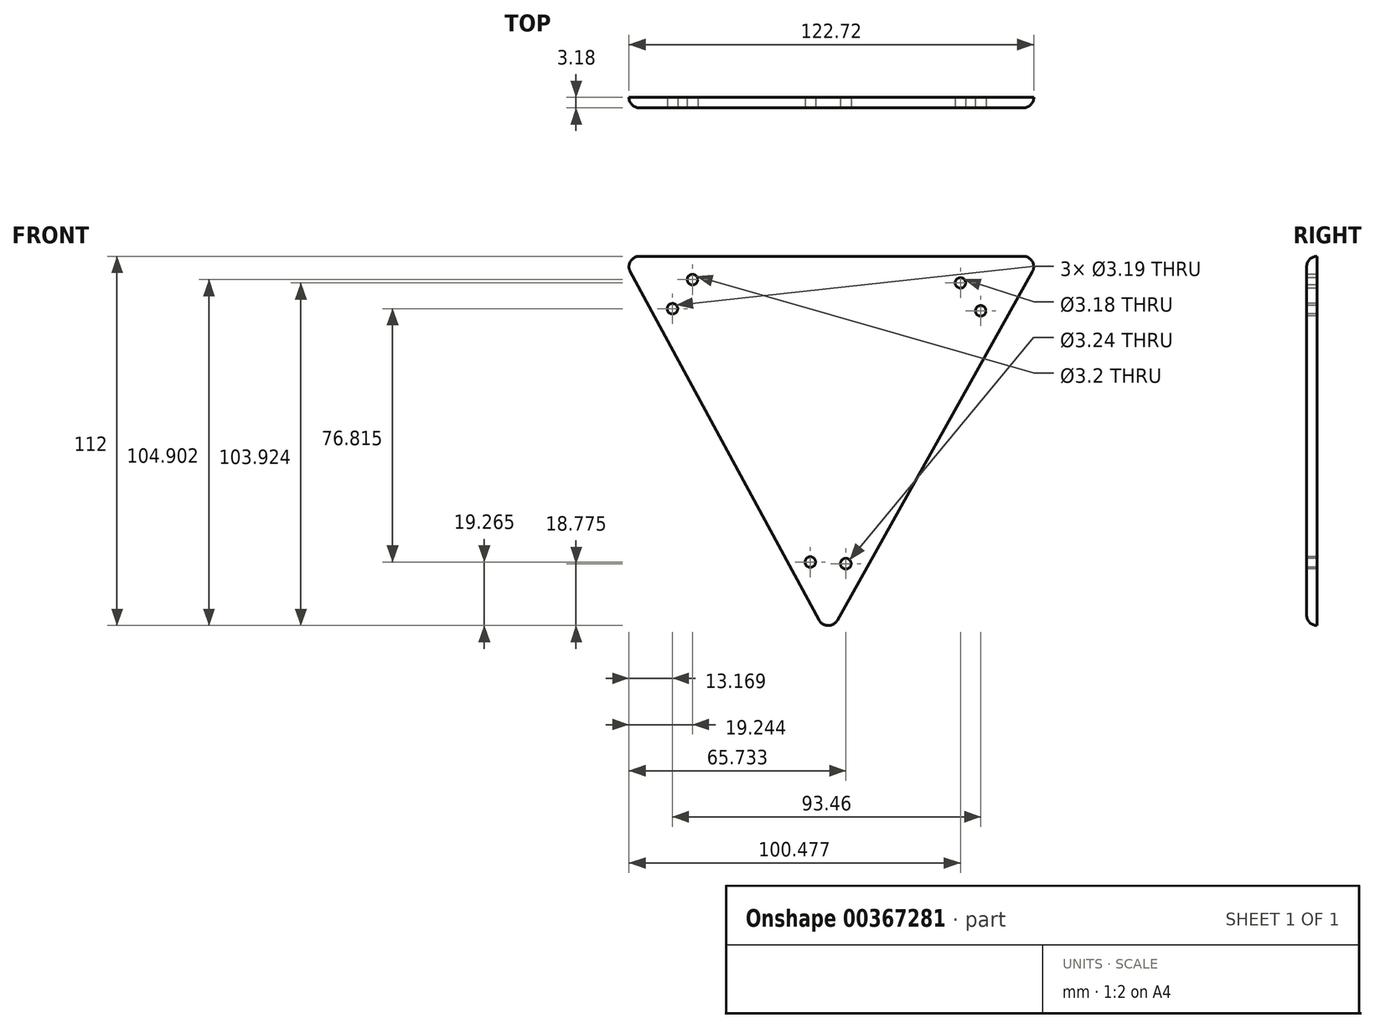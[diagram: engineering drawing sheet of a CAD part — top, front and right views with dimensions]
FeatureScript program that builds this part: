
annotation { "Feature Type Name" : "Feature", "Feature Type Description" : "" }
export const myFeature = defineFeature(function(context is Context, id is Id, definition is map)
    precondition{}
    {
        {
            var Q0;
            Q0=qCreatedBy(makeId("Front.planeOp"),FACE);
            var sketch = newSketch(context, id + "F0", { "sketchPlane" : qUnion([Q0])});
            skLineSegment(sketch, "E0", {"start": v(-62.51, 39.64) * mm, "end": v(64.6, 39.64) * mm});
            skLineSegment(sketch, "E1", {"start": v(64.6, 39.64) * mm, "end": v(0, -75.77) * mm});
            skLineSegment(sketch, "E2", {"start": v(-62.51, 39.64) * mm, "end": v(0, -75.77) * mm});
            skCircle(sketch, "E3", {"center": v(-41.1, 32.54) * mm, "radius": 1.6 * mm});
            skCircle(sketch, "E4", {"center": v(-47.18, 23.72) * mm, "radius": 1.6 * mm});
            skCircle(sketch, "E5", {"center": v(46.28, 23.1) * mm, "radius": 1.6 * mm});
            skCircle(sketch, "E6", {"center": v(5.38, -53.58) * mm, "radius": 1.62 * mm});
            skCircle(sketch, "E7", {"center": v(40.13, 31.56) * mm, "radius": 1.59 * mm});
            skCircle(sketch, "E8", {"center": v(7.83, 33.52) * mm, "radius": 1.58 * mm});
            skCircle(sketch, "E9", {"center": v(-5.38, -53.1) * mm, "radius": 1.6 * mm});
            skCircle(sketch, "E10", {"center": v(-6.85, 33.52) * mm, "radius": 1.57 * mm});
            skSolve(sketch);
        }
        {
            var Q0;
            Q0=qSketchRegion(id+"F0",true);
            var Q1;
            Q1=makeQuery(id+"F0.imprint","IMPRINT",FACE,{"disambiguationData":[TD([[makeQuery(id+"F0.imprint","IMPRINT",EDGE,{"derivedFrom":sQuery(id+"F0.wireOp",EDGE,"E8")}),1.0]])]});
            var Q2;
            Q2=makeQuery(id+"F0.imprint","IMPRINT",FACE,{"disambiguationData":[TD([[makeQuery(id+"F0.imprint","IMPRINT",EDGE,{"derivedFrom":sQuery(id+"F0.wireOp",EDGE,"E10")}),1.0]])]});
            extrude(context, id + "F1", {"entities" : qUnion([Q0, Q1, Q2]), "oppositeDirection" : true, "depth" : 3.17 * mm});
        }
        {
            var Q0;
            Q0=makeQuery(id+"F1.opExtrude","SWEPT_EDGE",EDGE,{"disambiguationData":[OSD([sQuery(id+"F0.wireOp",EDGE,"E0"),sQuery(id+"F0.wireOp",EDGE,"E1")])]});
            var Q1;
            Q1=makeQuery(id+"F1.opExtrude","SWEPT_EDGE",EDGE,{"disambiguationData":[OSD([sQuery(id+"F0.wireOp",EDGE,"E0"),sQuery(id+"F0.wireOp",EDGE,"E2")])]});
            var Q2;
            Q2=makeQuery(id+"F1.opExtrude","SWEPT_EDGE",EDGE,{"disambiguationData":[OSD([sQuery(id+"F0.wireOp",EDGE,"E1"),sQuery(id+"F0.wireOp",EDGE,"E2")])]});
            var Q3;
            Q3=makeQuery(id+"F1.opExtrude","CAP_EDGE",EDGE,{"disambiguationData":[OSD([sQuery(id+"F0.wireOp",EDGE,"E2")])],"isStart":true});
            var Q4;
            Q4=makeQuery(id+"F1.opExtrude","CAP_EDGE",EDGE,{"disambiguationData":[OSD([sQuery(id+"F0.wireOp",EDGE,"E1")])],"isStart":true});
            var Q5;
            Q5=makeQuery(id+"F1.opExtrude","CAP_EDGE",EDGE,{"disambiguationData":[OSD([sQuery(id+"F0.wireOp",EDGE,"E0")])],"isStart":true});
            fillet(context, id + "F2", {"entities" : qUnion([Q0, Q1, Q2, Q3, Q4, Q5]), "radius" : 3.17 * mm, "tangentPropagation" : true, "allowEdgeOverflow" : false});
        }
    });
